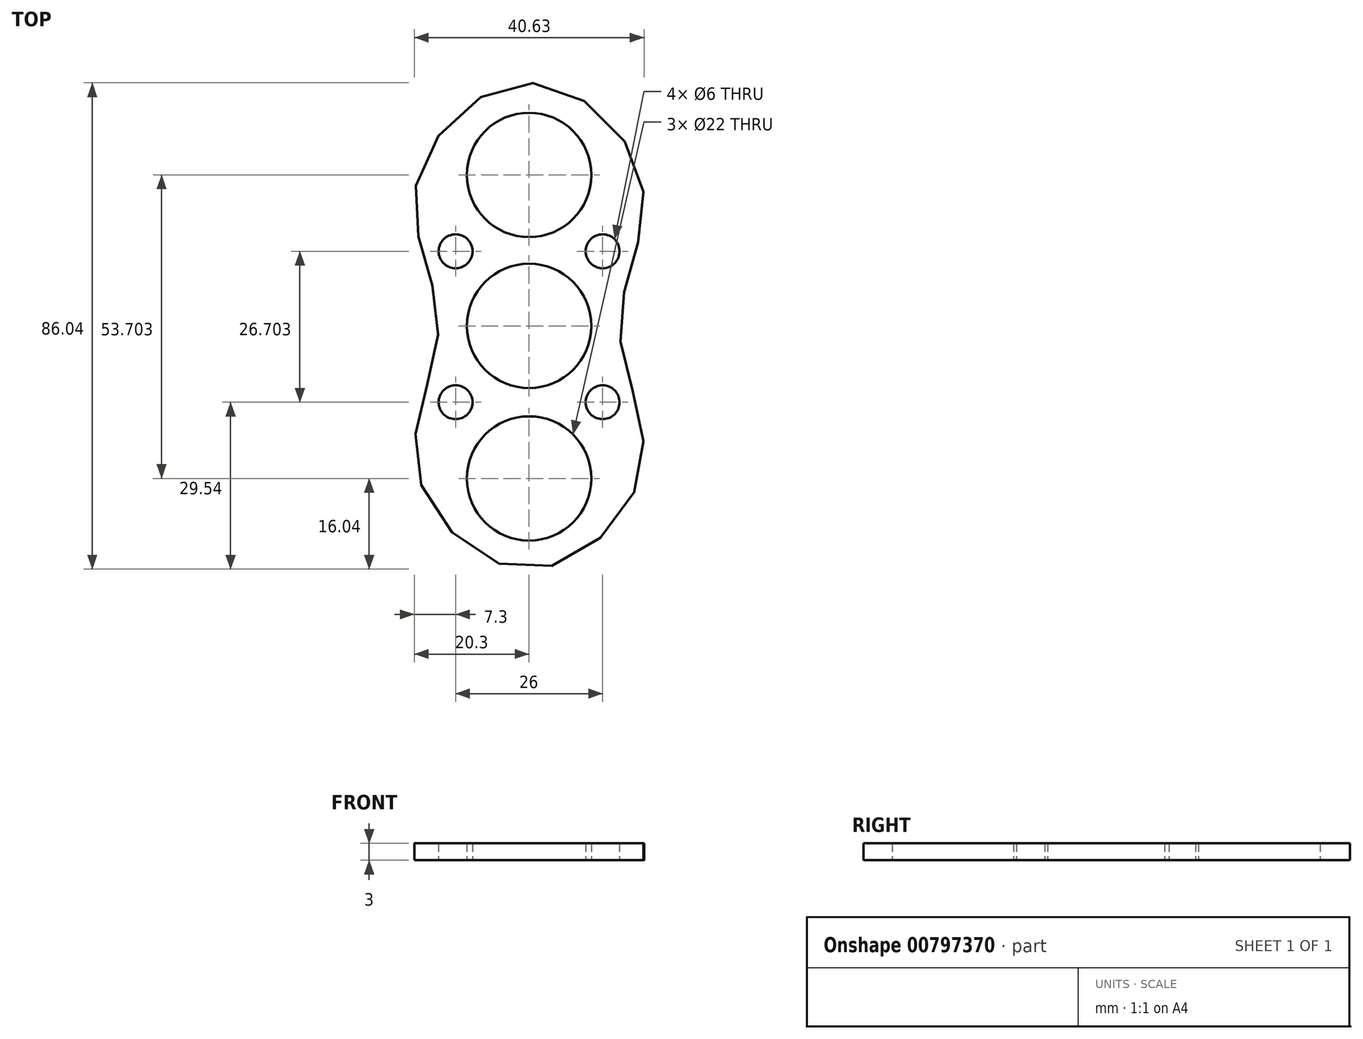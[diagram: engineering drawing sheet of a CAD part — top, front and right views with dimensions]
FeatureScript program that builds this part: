
annotation { "Feature Type Name" : "Feature", "Feature Type Description" : "" }
export const myFeature = defineFeature(function(context is Context, id is Id, definition is map)
    precondition{}
    {
        {
            var Q0;
            Q0=qCreatedBy(makeId("Top.planeOp"),FACE);
            var sketch = newSketch(context, id + "F0", { "sketchPlane" : qUnion([Q0])});
            skCircle(sketch, "E0", {"center": v(0, 0) * mm, "radius": 11 * mm});
            skFitSpline(sketch, "E1", {"points": [v(-20.04, 24.8) * mm, v(-16, 0.02) * mm, v(-19.98, -25) * mm, v(0, -43.04) * mm, v(19.98, -24.99) * mm, v(16, -0.02) * mm, v(20.05, 25.1) * mm, v(0, 43) * mm, v(-20.04, 24.8) * mm]});
            skCircle(sketch, "E2", {"center": v(0, 26.7) * mm, "radius": 11 * mm});
            skCircle(sketch, "E3", {"center": v(0, -27) * mm, "radius": 11 * mm});
            skCircle(sketch, "E4", {"center": v(13, 13.2) * mm, "radius": 3 * mm});
            skCircle(sketch, "E5", {"center": v(-13, 13.2) * mm, "radius": 3 * mm});
            skCircle(sketch, "E6", {"center": v(-13, -13.5) * mm, "radius": 3 * mm});
            skCircle(sketch, "E7", {"center": v(13, -13.5) * mm, "radius": 3 * mm});
            skSolve(sketch);
        }
        {
            var Q0;
            Q0 = qSketchRegion(id + "F0", true);
            extrude(context, id + "F1", {"entities" : qUnion([Q0]), "depth" : 3 * mm, "offsetDistance" : 25 * mm});
        }
    });
